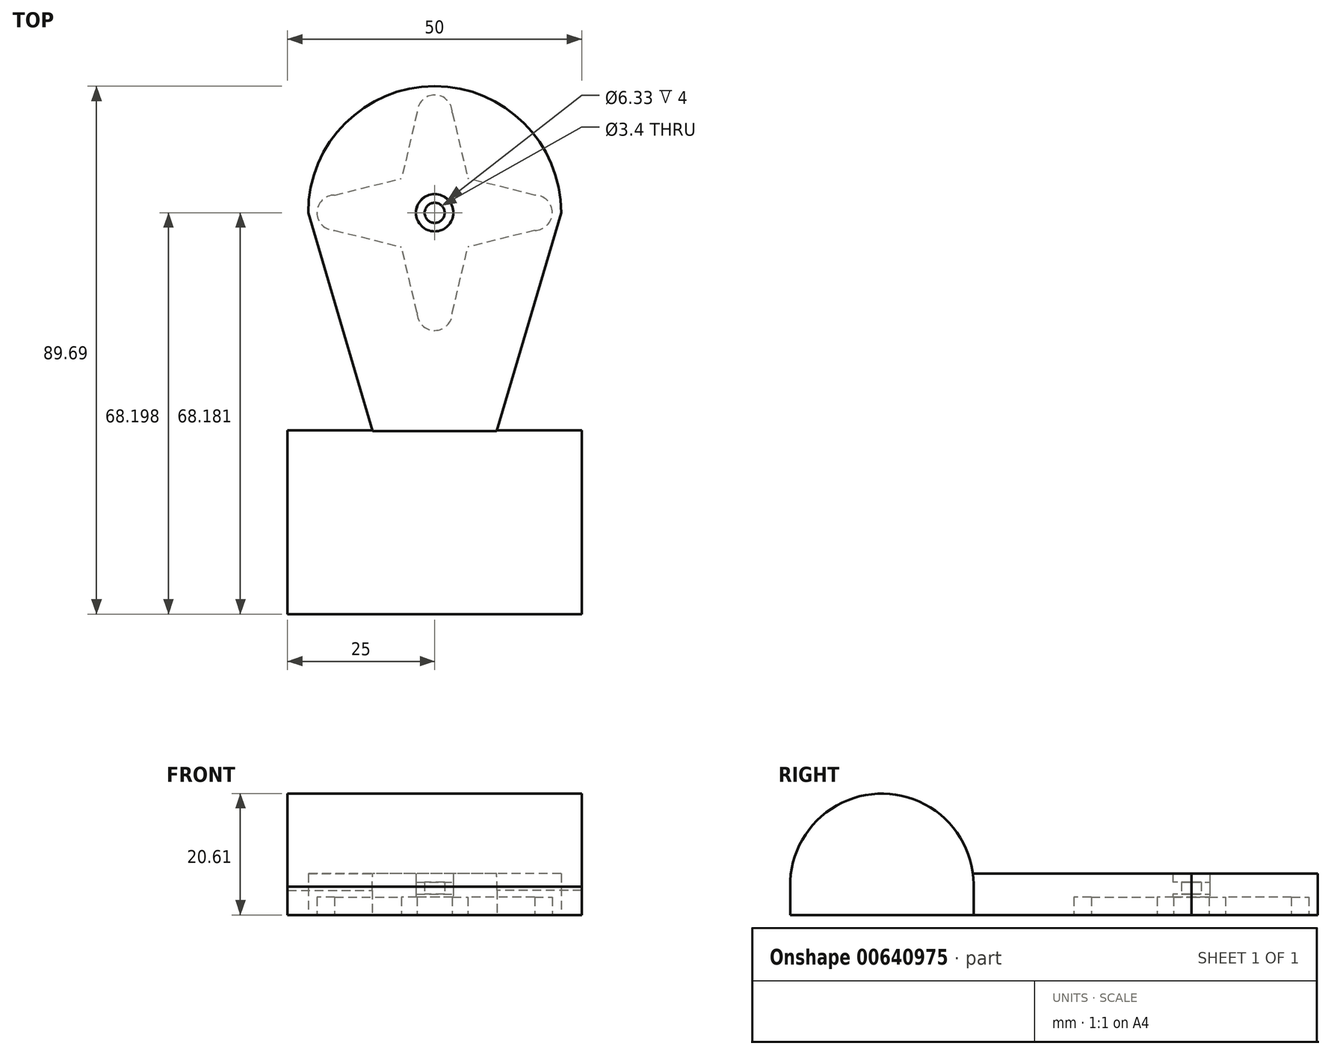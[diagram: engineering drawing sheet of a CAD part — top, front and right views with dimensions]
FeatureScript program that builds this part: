
annotation { "Feature Type Name" : "Feature", "Feature Type Description" : "" }
export const myFeature = defineFeature(function(context is Context, id is Id, definition is map)
    precondition{}
    {
        {
            var Q0;
            Q0=qCreatedBy(makeId("Top.planeOp"),FACE);
            var sketch = newSketch(context, id + "F0", { "sketchPlane" : qUnion([Q0])});
            skArc(sketch, "E0", {"start": v(21.5, 46.05) * mm, "mid": v(0, 67.54) * mm, "end": v(-21.5, 46.05) * mm});
            skLineSegment(sketch, "E1", {"start": v(35.96, 46.05) * mm, "end": v(-34.93, 46.05) * mm, "construction": true});
            skLineSegment(sketch, "E2", {"start": v(-21.5, 46.05) * mm, "end": v(-7.66, -0.86) * mm});
            skLineSegment(sketch, "E3.MirrorCS", {"start": v(21.5, 46.05) * mm, "end": v(7.66, -0.86) * mm});
            skLineSegment(sketch, "E4", {"start": v(-7.66, -0.86) * mm, "end": v(7.66, -0.86) * mm});
            skArc(sketch, "E5", {"start": v(17, 43.05) * mm, "mid": v(20, 46.05) * mm, "end": v(17, 49.05) * mm});
            skArc(sketch, "E6.MirrorC", {"start": v(-17, 43.05) * mm, "mid": v(-20, 46.05) * mm, "end": v(-17, 49.05) * mm});
            skArc(sketch, "E7", {"start": v(3, 63.05) * mm, "mid": v(0, 66.05) * mm, "end": v(-3, 63.05) * mm});
            skArc(sketch, "E8.MirrorC", {"start": v(3, 29.05) * mm, "mid": v(0, 26.05) * mm, "end": v(-3, 29.05) * mm});
            skLineSegment(sketch, "E9", {"start": v(-17, 43.05) * mm, "end": v(-5.64, 40.23) * mm});
            skLineSegment(sketch, "E10.MirrorCS", {"start": v(-17, 49.05) * mm, "end": v(-5.64, 51.86) * mm});
            skLineSegment(sketch, "E11.MirrorCS", {"start": v(17, 49.05) * mm, "end": v(5.64, 51.86) * mm});
            skLineSegment(sketch, "E12.MirrorCS", {"start": v(17, 43.05) * mm, "end": v(5.64, 40.23) * mm});
            skLineSegment(sketch, "E13", {"start": v(-3, 63.05) * mm, "end": v(-5.64, 51.86) * mm});
            skLineSegment(sketch, "E14.MirrorCS", {"start": v(3, 63.05) * mm, "end": v(5.64, 51.86) * mm});
            skLineSegment(sketch, "E15.MirrorCS", {"start": v(-3, 29.05) * mm, "end": v(-5.64, 40.23) * mm});
            skLineSegment(sketch, "E16.MirrorCS", {"start": v(3, 29.05) * mm, "end": v(5.64, 40.23) * mm});
            skPoint(sketch, "E17.orphan", {"position": v(-6.27, 49.15) * mm});
            skPoint(sketch, "E18.orphan", {"position": v(-1.68, 52.84) * mm});
            skPoint(sketch, "E19.orphan", {"position": v(1.68, 52.84) * mm});
            skPoint(sketch, "E20.orphan", {"position": v(6.27, 49.15) * mm});
            skPoint(sketch, "E21.orphan", {"position": v(6.27, 42.94) * mm});
            skPoint(sketch, "E22.orphan", {"position": v(1.68, 39.25) * mm});
            skPoint(sketch, "E23.orphan", {"position": v(-6.27, 42.94) * mm});
            skPoint(sketch, "E24.orphan", {"position": v(-1.68, 39.25) * mm});
            skCircle(sketch, "E25", {"center": v(0, 46.05) * mm, "radius": 3.17 * mm});
            skCircle(sketch, "E26", {"center": v(0, 46.05) * mm, "radius": 1.7 * mm});
            skSolve(sketch);
        }
        {
            var Q0;
            Q0=makeQuery(id+"F0.imprint","IMPRINT",FACE,{"disambiguationData":[TD([[makeQuery(id+"F0.imprint","IMPRINT",EDGE,{"derivedFrom":sQuery(id+"F0.wireOp",EDGE,"E5")}),1.0]])]});
            var Q1;
            Q1=makeQuery(id+"F0.imprint","IMPRINT",FACE,{"disambiguationData":[TD([[makeQuery(id+"F0.imprint","IMPRINT",EDGE,{"derivedFrom":sQuery(id+"F0.wireOp",EDGE,"E0")}),1.0]])]});
            extrude(context, id + "F1", {"entities" : qUnion([Q0, Q1]), "depth" : 7 * mm, "offsetDistance" : 25.4 * mm});
        }
        {
            var Q0;
            Q0=qCreatedBy(makeId("Right.planeOp"),FACE);
            var sketch = newSketch(context, id + "F2", { "sketchPlane" : qUnion([Q0])});
            skArc(sketch, "E27", {"start": v(9.03, 4.77) * mm, "mid": v(9.04, 4.8) * mm, "end": v(9.05, 4.85) * mm});
            skLineSegment(sketch, "E28.bottom", {"start": v(9.03, 0) * mm, "end": v(-22.15, 0) * mm});
            skLineSegment(sketch, "E28.top", {"start": v(9.03, 4.77) * mm, "end": v(-22.15, 4.77) * mm});
            skLineSegment(sketch, "E28.left", {"start": v(9.03, 0) * mm, "end": v(9.03, 4.77) * mm});
            skLineSegment(sketch, "E28.right", {"start": v(-22.15, 0) * mm, "end": v(-22.15, 4.77) * mm});
            skPoint(sketch, "E28.middle", {"position": v(-6.56, 2.39) * mm});
            skArc(sketch, "E29", {"start": v(9.03, 4.17) * mm, "mid": v(-6.25, 20.6) * mm, "end": v(-22.15, 4.77) * mm});
            skPoint(sketch, "E29.second.point", {"position": v(9.03, 4.17) * mm});
            skPoint(sketch, "E29.third.point", {"position": v(5.24, -5.22) * mm});
            skSolve(sketch);
        }
        {
            var Q0;
            Q0 = qSketchRegion(id + "F2", true);
            extrude(context, id + "F3", {"entities" : qUnion([Q0]), "operationType" : NewBodyOperationType.ADD, "depth" : 25 * mm, "offsetDistance" : 25.4 * mm});
        }
        {
            var Q0;
            Q0=makeQuery(id+"F1.opExtrude","SWEPT_BODY",BODY,{"disambiguationData":[OSD([sQuery(id+"F0.wireOp",EDGE,"E0"),sQuery(id+"F0.wireOp",EDGE,"E2"),sQuery(id+"F0.wireOp",EDGE,"E3.MirrorCS"),sQuery(id+"F0.wireOp",EDGE,"E4")])]});
            var Q1;
            Q1=qCreatedBy(makeId("Right.planeOp"),FACE);
            mirror(context, id + "F4", {"operationType" : NewBodyOperationType.ADD, "entities" : qUnion([Q0]), "mirrorPlane" : qUnion([Q1])});
        }
        {
            var Q0;
            Q0=makeQuery(id+"F0.imprint","IMPRINT",FACE,{"disambiguationData":[TD([[makeQuery(id+"F0.imprint","IMPRINT",EDGE,{"derivedFrom":sQuery(id+"F0.wireOp",EDGE,"E5")}),1.0]])]});
            extrude(context, id + "F5", {"entities" : qUnion([Q0]), "operationType" : NewBodyOperationType.REMOVE, "depth" : 3 * mm, "offsetDistance" : 25.4 * mm});
        }
        {
            var Q0;
            Q0=qCreatedBy(makeId("Top.planeOp"),FACE);
            cPlane(context, id + "F6", {"entities" : qUnion([Q0]), "cplaneType" : CPlaneType.OFFSET, "offset" : 3.56 * mm, "width" : 152.4 * mm, "height" : 152.4 * mm});
        }
        {
            var Q0;
            Q0=qCreatedBy(id+"F6.planeOp",FACE);
            var sketch = newSketch(context, id + "F7", { "sketchPlane" : qUnion([Q0])});
            skCircle(sketch, "E30", {"center": v(0, 46.03) * mm, "radius": 3.17 * mm});
            skCircle(sketch, "E31", {"center": v(0, 46.03) * mm, "radius": 1.7 * mm});
            skSolve(sketch);
        }
        {
            var Q0;
            Q0=makeQuery(id+"F7.imprint","IMPRINT",FACE,{"disambiguationData":[TD([[makeQuery(id+"F7.imprint","IMPRINT",EDGE,{"derivedFrom":sQuery(id+"F7.wireOp",EDGE,"E30")}),1.0]])]});
            extrude(context, id + "F8", {"entities" : qUnion([Q0]), "operationType" : NewBodyOperationType.ADD, "depth" : 2 * mm, "offsetDistance" : 25.4 * mm});
        }
    });
